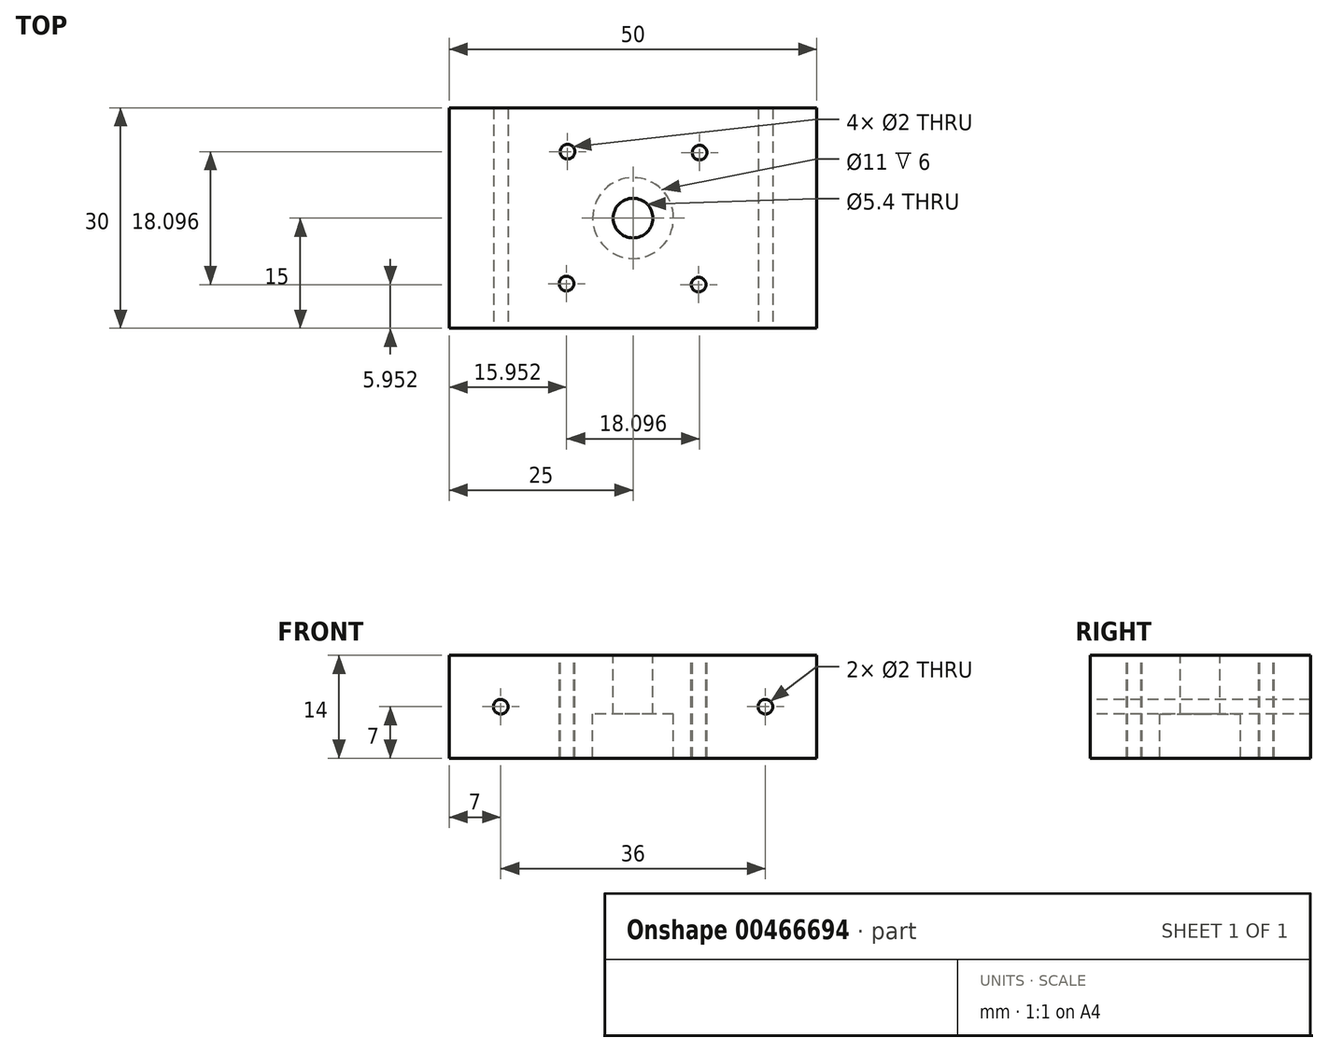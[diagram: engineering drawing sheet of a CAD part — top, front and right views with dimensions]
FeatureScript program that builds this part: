
annotation { "Feature Type Name" : "Feature", "Feature Type Description" : "" }
export const myFeature = defineFeature(function(context is Context, id is Id, definition is map)
    precondition{}
    {
        {
            var Q0;
            Q0=qCreatedBy(makeId("Top.planeOp"),FACE);
            var sketch = newSketch(context, id + "F0", { "sketchPlane" : qUnion([Q0])});
            skLineSegment(sketch, "E0.bottom", {"start": v(25, 15) * mm, "end": v(-25, 15) * mm});
            skLineSegment(sketch, "E0.top", {"start": v(25, -15) * mm, "end": v(-25, -15) * mm});
            skLineSegment(sketch, "E0.left", {"start": v(25, 15) * mm, "end": v(25, -15) * mm});
            skLineSegment(sketch, "E0.right", {"start": v(-25, 15) * mm, "end": v(-25, -15) * mm});
            skPoint(sketch, "E0.middle", {"position": v(0, 0) * mm});
            skSolve(sketch);
        }
        {
            var Q0;
            Q0=makeQuery(id+"F0.imprint","IMPRINT",FACE,{"disambiguationData":[TD([[makeQuery(id+"F0.imprint","IMPRINT",EDGE,{"derivedFrom":sQuery(id+"F0.wireOp",EDGE,"E0.bottom")}),1.0]])]});
            extrude(context, id + "F1", {"entities" : qUnion([Q0]), "depth" : 14 * mm});
        }
        {
            var Q0;
            Q0=makeQuery(id+"F1.opExtrude","CAP_FACE",FACE,{"disambiguationData":[OSD([sQuery(id+"F0.wireOp",EDGE,"E0.bottom"),sQuery(id+"F0.wireOp",EDGE,"E0.top"),sQuery(id+"F0.wireOp",EDGE,"E0.left"),sQuery(id+"F0.wireOp",EDGE,"E0.right")])],"isStart":false});
            var sketch = newSketch(context, id + "F2", { "sketchPlane" : qUnion([Q0])});
            skPoint(sketch, "E1", {"position": v(0, 0) * mm});
            skSolve(sketch);
        }
        {
            var Q0;
            Q0=sQuery(id+"F2.wireOp",VERTEX,"E1");
            var Q1;
            Q1=makeQuery(id+"F1.opExtrude","SWEPT_BODY",BODY,{"disambiguationData":[OSD([sQuery(id+"F0.wireOp",EDGE,"E0.bottom"),sQuery(id+"F0.wireOp",EDGE,"E0.top"),sQuery(id+"F0.wireOp",EDGE,"E0.left"),sQuery(id+"F0.wireOp",EDGE,"E0.right")])]});
            hole(context, id + "F3", {"style" : HoleStyle.SIMPLE, "endStyle" : HoleEndStyle.THROUGH, "holeDiameter" : 11 * mm, "isTappedThrough" : true, "tappedDepth" : 12 * mm, "tapClearance" : 3, "locations" : qUnion([Q0]), "scope" : qUnion([Q1])});
        }
        {
            var Q0;
            Q0=makeQuery(id+"F1.opExtrude","CAP_FACE",FACE,{"disambiguationData":[OSD([sQuery(id+"F0.wireOp",EDGE,"E0.bottom"),sQuery(id+"F0.wireOp",EDGE,"E0.top"),sQuery(id+"F0.wireOp",EDGE,"E0.left"),sQuery(id+"F0.wireOp",EDGE,"E0.right")])],"isStart":false});
            var sketch = newSketch(context, id + "F4", { "sketchPlane" : qUnion([Q0])});
            skPoint(sketch, "E2", {"position": v(0, 0) * mm});
            skCircle(sketch, "E3", {"center": v(0, 0) * mm, "radius": 6.2 * mm});
            skCircle(sketch, "E4", {"center": v(0, 0) * mm, "radius": 8 * mm});
            skCircle(sketch, "E5", {"center": v(0, 0) * mm, "radius": 11 * mm});
            skCircle(sketch, "E6", {"center": v(0, 0) * mm, "radius": 12.7 * mm});
            skPoint(sketch, "E7", {"position": v(8.91, -9.05) * mm});
            skPoint(sketch, "E8", {"position": v(-9.05, -8.91) * mm});
            skPoint(sketch, "E9", {"position": v(-8.91, 9.05) * mm});
            skPoint(sketch, "E10", {"position": v(9.05, 8.91) * mm});
            skSolve(sketch);
        }
        {
            var Q0;
            Q0=sQuery(id+"F4.wireOp",VERTEX,"4cb23bda-bb00-4eea-a839-b8acd72178f6");
            var Q1;
            Q1=sQuery(id+"F4.wireOp",VERTEX,"6a5fe324-0c00-4b74-974d-ec828e3f4cd3");
            var Q2;
            Q2=sQuery(id+"F4.wireOp",VERTEX,"E9");
            var Q3;
            Q3=sQuery(id+"F4.wireOp",VERTEX,"E10");
            var Q4;
            Q4=sQuery(id+"F4.wireOp",VERTEX,"E7");
            var Q5;
            Q5=sQuery(id+"F4.wireOp",VERTEX,"E8");
            var Q6;
            Q6=makeQuery(id+"F1.opExtrude","SWEPT_BODY",BODY,{"disambiguationData":[OSD([sQuery(id+"F0.wireOp",EDGE,"E0.bottom"),sQuery(id+"F0.wireOp",EDGE,"E0.top"),sQuery(id+"F0.wireOp",EDGE,"E0.left"),sQuery(id+"F0.wireOp",EDGE,"E0.right")])]});
            hole(context, id + "F5", {"style" : HoleStyle.SIMPLE, "endStyle" : HoleEndStyle.THROUGH, "holeDiameter" : 2 * mm, "isTappedThrough" : true, "tappedDepth" : 12 * mm, "tapClearance" : 3, "locations" : qUnion([Q0, Q1, Q2, Q3, Q4, Q5]), "scope" : qUnion([Q6])});
        }
        {
            var Q0;
            Q0=makeQuery(id+"F1.opExtrude","SWEPT_FACE",FACE,{"disambiguationData":[OSD([sQuery(id+"F0.wireOp",EDGE,"E0.top")])]});
            var sketch = newSketch(context, id + "F6", { "sketchPlane" : qUnion([Q0])});
            skPoint(sketch, "E11", {"position": v(18, 7) * mm});
            skPoint(sketch, "E11.positionSnap0", {"position": v(25, 7) * mm});
            skPoint(sketch, "E12", {"position": v(-18, 7) * mm});
            skSolve(sketch);
        }
        {
            var Q0;
            Q0=sQuery(id+"F6.wireOp",VERTEX,"E11");
            var Q1;
            Q1=sQuery(id+"F6.wireOp",VERTEX,"E12");
            var Q2;
            Q2=makeQuery(id+"F1.opExtrude","SWEPT_BODY",BODY,{"disambiguationData":[OSD([sQuery(id+"F0.wireOp",EDGE,"E0.bottom"),sQuery(id+"F0.wireOp",EDGE,"E0.top"),sQuery(id+"F0.wireOp",EDGE,"E0.left"),sQuery(id+"F0.wireOp",EDGE,"E0.right")])]});
            hole(context, id + "F7", {"style" : HoleStyle.SIMPLE, "endStyle" : HoleEndStyle.THROUGH, "holeDiameter" : 2 * mm, "isTappedThrough" : true, "tappedDepth" : 12 * mm, "tapClearance" : 3, "locations" : qUnion([Q0, Q1]), "scope" : qUnion([Q2])});
        }
        {
            var Q0;
            Q0=makeQuery(id+"F1.opExtrude","CAP_FACE",FACE,{"disambiguationData":[OSD([sQuery(id+"F0.wireOp",EDGE,"E0.bottom"),sQuery(id+"F0.wireOp",EDGE,"E0.top"),sQuery(id+"F0.wireOp",EDGE,"E0.left"),sQuery(id+"F0.wireOp",EDGE,"E0.right")])],"isStart":false});
            var sketch = newSketch(context, id + "F8", { "sketchPlane" : qUnion([Q0])});
            skCircle(sketch, "E13", {"center": v(0, 0) * mm, "radius": 5.5 * mm});
            skCircle(sketch, "E14.0", {"center": v(0, 0) * mm, "radius": 2.7 * mm});
            skSolve(sketch);
        }
        {
            var Q0;
            Q0 = qSketchRegion(id + "F8", true);
            extrude(context, id + "F9", {"entities" : qUnion([Q0]), "operationType" : NewBodyOperationType.ADD, "oppositeDirection" : true, "depth" : 8 * mm});
        }
    });
